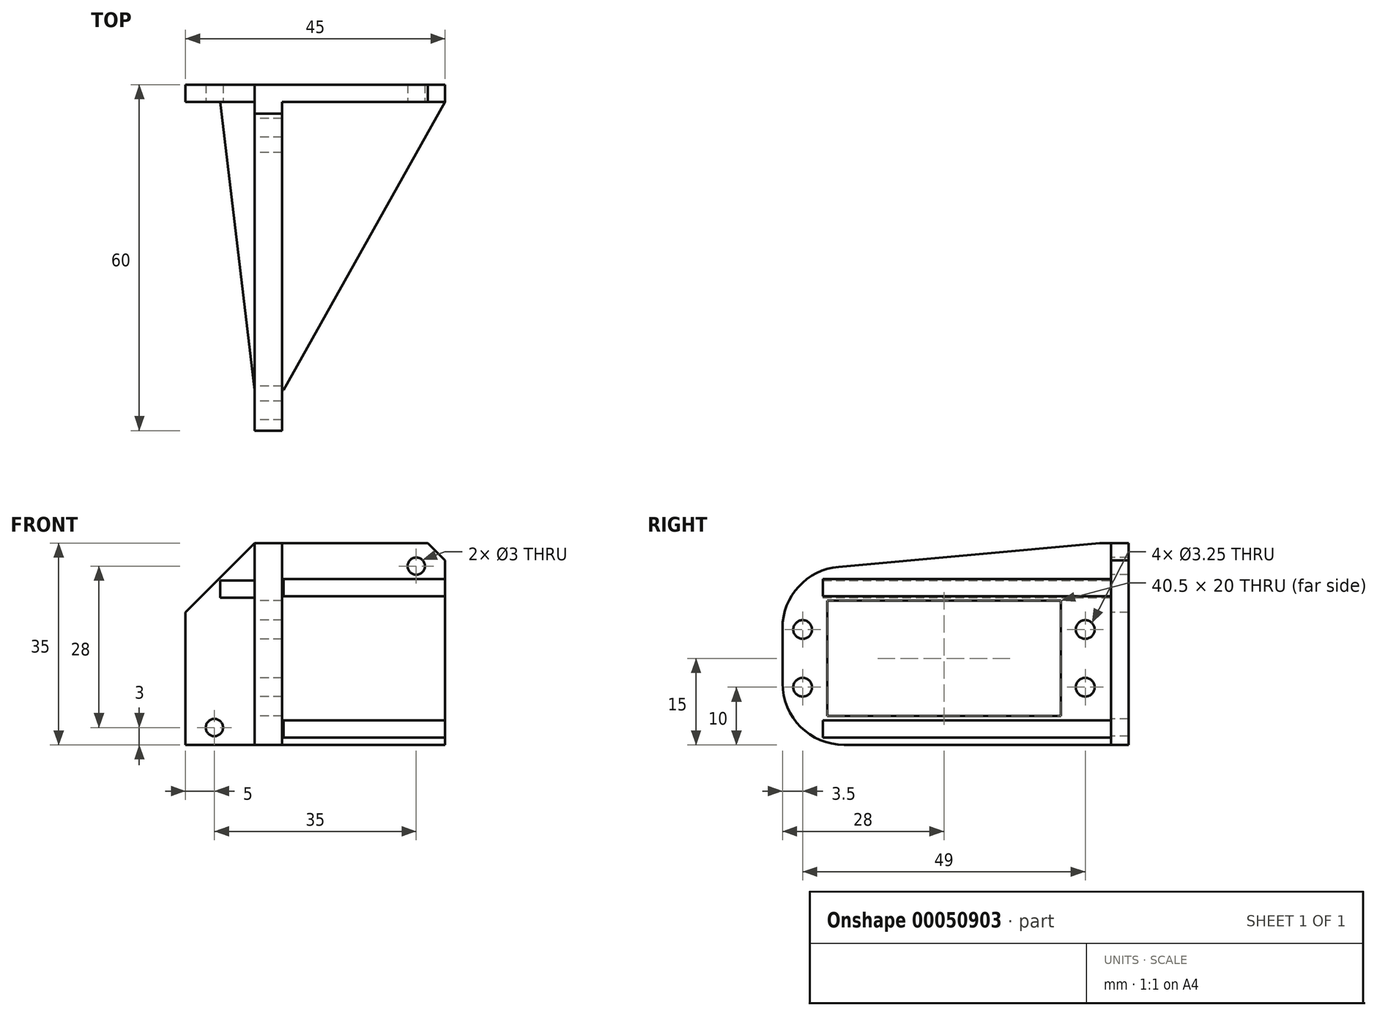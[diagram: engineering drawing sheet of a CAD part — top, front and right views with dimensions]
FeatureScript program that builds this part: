
annotation { "Feature Type Name" : "Feature", "Feature Type Description" : "" }
export const myFeature = defineFeature(function(context is Context, id is Id, definition is map)
    precondition{}
    {
        {
            var Q0;
            Q0=qCreatedBy(makeId("Front.planeOp"),FACE);
            var sketch = newSketch(context, id + "F0", { "sketchPlane" : qUnion([Q0])});
            skLineSegment(sketch, "E0", {"start": v(-22.5, 0) * mm, "end": v(22.5, 0) * mm});
            skLineSegment(sketch, "E1", {"start": v(22.5, 0) * mm, "end": v(22.5, 32) * mm});
            skLineSegment(sketch, "E2", {"start": v(22.5, 32) * mm, "end": v(19.5, 35) * mm});
            skLineSegment(sketch, "E3", {"start": v(19.5, 35) * mm, "end": v(-10.5, 35) * mm});
            skLineSegment(sketch, "E4", {"start": v(-10.5, 35) * mm, "end": v(-22.5, 23) * mm});
            skLineSegment(sketch, "E5", {"start": v(-22.5, 23) * mm, "end": v(-22.5, 0) * mm});
            skCircle(sketch, "E6", {"center": v(17.5, 31) * mm, "radius": 1.5 * mm});
            skCircle(sketch, "E7", {"center": v(-17.5, 3) * mm, "radius": 1.5 * mm});
            skSolve(sketch);
        }
        {
            var Q0;
            Q0=makeQuery(id+"F0.imprint","IMPRINT",FACE,{"disambiguationData":[TD([[makeQuery(id+"F0.imprint","IMPRINT",EDGE,{"derivedFrom":sQuery(id+"F0.wireOp",EDGE,"E0")}),1.0]])]});
            extrude(context, id + "F1", {"entities" : qUnion([Q0]), "oppositeDirection" : true, "depth" : 3 * mm});
        }
        {
            var Q0;
            Q0=makeQuery(id+"F1.opExtrude","CAP_FACE",FACE,{"disambiguationData":[OSD([sQuery(id+"F0.wireOp",EDGE,"E0"),sQuery(id+"F0.wireOp",EDGE,"E1"),sQuery(id+"F0.wireOp",EDGE,"E2"),sQuery(id+"F0.wireOp",EDGE,"E3"),sQuery(id+"F0.wireOp",EDGE,"E4"),sQuery(id+"F0.wireOp",EDGE,"E5"),sQuery(id+"F0.wireOp",EDGE,"E6"),sQuery(id+"F0.wireOp",EDGE,"E7")])],"isStart":true});
            var sketch = newSketch(context, id + "F2", { "sketchPlane" : qUnion([Q0])});
            skLineSegment(sketch, "E8.bottom", {"start": v(-10.5, 35) * mm, "end": v(-5.77, 35) * mm});
            skLineSegment(sketch, "E8.top", {"start": v(-10.5, 0) * mm, "end": v(-5.77, 0) * mm});
            skLineSegment(sketch, "E8.left", {"start": v(-10.5, 35) * mm, "end": v(-10.5, 0) * mm});
            skLineSegment(sketch, "E8.right", {"start": v(-5.77, 35) * mm, "end": v(-5.77, 0) * mm});
            skLineSegment(sketch, "E9", {"start": v(-5.77, 25.75) * mm, "end": v(22.5, 25.75) * mm});
            skLineSegment(sketch, "E10", {"start": v(22.5, 25.75) * mm, "end": v(22.5, 28.75) * mm});
            skLineSegment(sketch, "E11", {"start": v(22.5, 28.75) * mm, "end": v(-5.77, 28.75) * mm});
            skLineSegment(sketch, "E12", {"start": v(-5.77, 4.25) * mm, "end": v(22.5, 4.25) * mm});
            skLineSegment(sketch, "E13", {"start": v(22.5, 4.25) * mm, "end": v(22.5, 1.25) * mm});
            skLineSegment(sketch, "E14", {"start": v(22.5, 1.25) * mm, "end": v(-5.77, 1.25) * mm});
            skSolve(sketch);
        }
        {
            var Q0;
            Q0=makeQuery(id+"F2.imprint","IMPRINT",FACE,{"disambiguationData":[TD([[makeQuery(id+"F2.imprint","IMPRINT",EDGE,{"derivedFrom":sQuery(id+"F2.wireOp",EDGE,"E8.bottom")}),1.0]])]});
            extrude(context, id + "F3", {"entities" : qUnion([Q0]), "operationType" : NewBodyOperationType.ADD, "depth" : 57 * mm});
        }
        {
            var Q0;
            Q0=makeQuery(id+"F3.opExtrude","SWEPT_FACE",FACE,{"disambiguationData":[OSD([sQuery(id+"F2.wireOp",EDGE,"E8.left")])]});
            var sketch = newSketch(context, id + "F4", { "sketchPlane" : qUnion([Q0])});
            skLineSegment(sketch, "E15.bottom", {"start": v(8.75, 5) * mm, "end": v(49.25, 5) * mm});
            skLineSegment(sketch, "E15.top", {"start": v(8.75, 25) * mm, "end": v(49.25, 25) * mm});
            skLineSegment(sketch, "E15.left", {"start": v(8.75, 5) * mm, "end": v(8.75, 25) * mm});
            skLineSegment(sketch, "E15.right", {"start": v(49.25, 5) * mm, "end": v(49.25, 25) * mm});
            skCircle(sketch, "E16", {"center": v(4.5, 20) * mm, "radius": 1.63 * mm});
            skCircle(sketch, "E17", {"center": v(4.5, 10) * mm, "radius": 1.63 * mm});
            skCircle(sketch, "E18", {"center": v(53.5, 20) * mm, "radius": 1.63 * mm});
            skCircle(sketch, "E19", {"center": v(53.5, 10) * mm, "radius": 1.63 * mm});
            skLineSegment(sketch, "E20", {"start": v(8.75, 15) * mm, "end": v(1.08, 15) * mm, "construction": true});
            skLineSegment(sketch, "E21", {"start": v(1.08, 15) * mm, "end": v(55, 15) * mm, "construction": true});
            skLineSegment(sketch, "E22", {"start": v(29, 25) * mm, "end": v(29, 5) * mm, "construction": true});
            skSolve(sketch);
        }
        {
            var Q0;
            Q0=makeQuery(id+"F4.imprint","IMPRINT",FACE,{"disambiguationData":[TD([[makeQuery(id+"F4.imprint","IMPRINT",EDGE,{"derivedFrom":sQuery(id+"F4.wireOp",EDGE,"E16")}),1.0]])]});
            var Q1;
            Q1=makeQuery(id+"F4.imprint","IMPRINT",FACE,{"disambiguationData":[TD([[makeQuery(id+"F4.imprint","IMPRINT",EDGE,{"derivedFrom":sQuery(id+"F4.wireOp",EDGE,"E17")}),1.0]])]});
            var Q2;
            Q2=makeQuery(id+"F4.imprint","IMPRINT",FACE,{"disambiguationData":[TD([[makeQuery(id+"F4.imprint","IMPRINT",EDGE,{"derivedFrom":sQuery(id+"F4.wireOp",EDGE,"E15.bottom")}),1.0]])]});
            var Q3;
            Q3=makeQuery(id+"F4.imprint","IMPRINT",FACE,{"disambiguationData":[TD([[makeQuery(id+"F4.imprint","IMPRINT",EDGE,{"derivedFrom":sQuery(id+"F4.wireOp",EDGE,"E18")}),1.0]])]});
            var Q4;
            Q4=makeQuery(id+"F4.imprint","IMPRINT",FACE,{"disambiguationData":[TD([[makeQuery(id+"F4.imprint","IMPRINT",EDGE,{"derivedFrom":sQuery(id+"F4.wireOp",EDGE,"E19")}),1.0]])]});
            extrude(context, id + "F5", {"entities" : qUnion([Q0, Q1, Q2, Q3, Q4]), "operationType" : NewBodyOperationType.REMOVE, "endBound" : BoundingType.THROUGH_ALL, "oppositeDirection" : true, "depth" : 25 * mm});
        }
        {
            var Q0;
            {var subQ0=sQuery(id+"F2.wireOp",EDGE,"E9");Q0=makeQuery(id+"F2.imprint","IMPRINT",FACE,{"disambiguationData":[TD([[makeQuery(id+"F2.imprint","IMPRINT",EDGE,{"derivedFrom":subQ0}),1.0]])]});}
            var Q1;
            {var subQ0=sQuery(id+"F2.wireOp",EDGE,"E12");Q1=makeQuery(id+"F2.imprint","IMPRINT",FACE,{"disambiguationData":[TD([[makeQuery(id+"F2.imprint","IMPRINT",EDGE,{"derivedFrom":subQ0}),-1.0]])]});}
            extrude(context, id + "F6", {"entities" : qUnion([Q0, Q1]), "operationType" : NewBodyOperationType.ADD, "depth" : 50 * mm});
        }
        {
            var Q0;
            Q0=makeQuery(id+"F6.opExtrude","CAP_EDGE",EDGE,{"disambiguationData":[OSD([sQuery(id+"F2.wireOp",EDGE,"E10")])],"isStart":false});
            var Q1;
            Q1=makeQuery(id+"F6.opExtrude","CAP_EDGE",EDGE,{"disambiguationData":[OSD([sQuery(id+"F2.wireOp",EDGE,"E13")])],"isStart":false});
            chamfer(context, id + "F7", {"entities" : qUnion([Q0, Q1]), "chamferType" : ChamferType.TWO_OFFSETS, "width1" : 28 * mm, "oppositeDirection" : false, "width2" : 50 * mm, "tangentPropagation" : true});
        }
        {
            var Q0;
            Q0=makeQuery(id+"F3.opExtrude","CAP_EDGE",EDGE,{"disambiguationData":[OSD([sQuery(id+"F2.wireOp",EDGE,"E8.bottom")])],"isStart":false});
            chamfer(context, id + "F8", {"entities" : qUnion([Q0]), "chamferType" : ChamferType.TWO_OFFSETS, "width1" : 5 * mm, "oppositeDirection" : false, "width2" : 55 * mm, "tangentPropagation" : true});
        }
        {
            var Q0;
            {var subQ0=sQuery(id+"F2.wireOp",EDGE,"E8.bottom");Q0=makeQuery(id+"F8.opChamfer","BLEND_EDGE",EDGE,{"blendedFrom":[makeQuery(id+"F3.opExtrude","CAP_EDGE",EDGE,{"disambiguationData":[OSD([subQ0])],"isStart":false}),makeQuery(id+"F3.opExtrude","CAP_FACE",FACE,{"disambiguationData":[OSD([subQ0,sQuery(id+"F2.wireOp",EDGE,"E8.top"),sQuery(id+"F2.wireOp",EDGE,"E8.left"),sQuery(id+"F2.wireOp",EDGE,"E8.right")])],"isStart":false})],"blendedInto":[makeQuery(id+"F3.opExtrude","CAP_FACE",FACE,{"disambiguationData":[OSD([subQ0,sQuery(id+"F2.wireOp",EDGE,"E8.top"),sQuery(id+"F2.wireOp",EDGE,"E8.left"),sQuery(id+"F2.wireOp",EDGE,"E8.right")])],"isStart":false})]});}
            var Q1;
            Q1=makeQuery(id+"F3.opExtrude","CAP_EDGE",EDGE,{"disambiguationData":[OSD([sQuery(id+"F2.wireOp",EDGE,"E8.top")])],"isStart":false});
            fillet(context, id + "F9", {"entities" : qUnion([Q0, Q1]), "radius" : 10.7 * mm, "tangentPropagation" : true, "allowEdgeOverflow" : false});
        }
        {
            var Q0;
            {var subQ1=sQuery(id+"F2.wireOp",EDGE,"E8.left");Q0=makeQuery(id+"F2.imprint","IMPRINT",FACE,{"disambiguationData":[TD([[makeQuery(id+"F2.imprint","IMPRINT",EDGE,{"derivedFrom":subQ1}),-1.0]])]});}
            var sketch = newSketch(context, id + "F10", { "sketchPlane" : qUnion([Q0])});
            skLineSegment(sketch, "E23.bottom", {"start": v(-10.5, 25.5) * mm, "end": v(-16.5, 25.5) * mm});
            skLineSegment(sketch, "E23.top", {"start": v(-10.5, 28.5) * mm, "end": v(-16.5, 28.5) * mm});
            skLineSegment(sketch, "E23.left", {"start": v(-10.5, 25.5) * mm, "end": v(-10.5, 28.5) * mm});
            skLineSegment(sketch, "E23.right", {"start": v(-16.5, 25.5) * mm, "end": v(-16.5, 28.5) * mm});
            skSolve(sketch);
        }
        {
            var Q0;
            Q0 = qSketchRegion(id + "F10", true);
            extrude(context, id + "F11", {"entities" : qUnion([Q0]), "operationType" : NewBodyOperationType.ADD, "depth" : 50 * mm});
        }
        {
            var Q0;
            Q0=makeQuery(id+"F11.opExtrude","CAP_EDGE",EDGE,{"disambiguationData":[OSD([sQuery(id+"F10.wireOp",EDGE,"E23.right")])],"isStart":false});
            chamfer(context, id + "F12", {"entities" : qUnion([Q0]), "chamferType" : ChamferType.TWO_OFFSETS, "width1" : 6 * mm, "oppositeDirection" : true, "width2" : 50 * mm, "tangentPropagation" : true});
        }
    });
